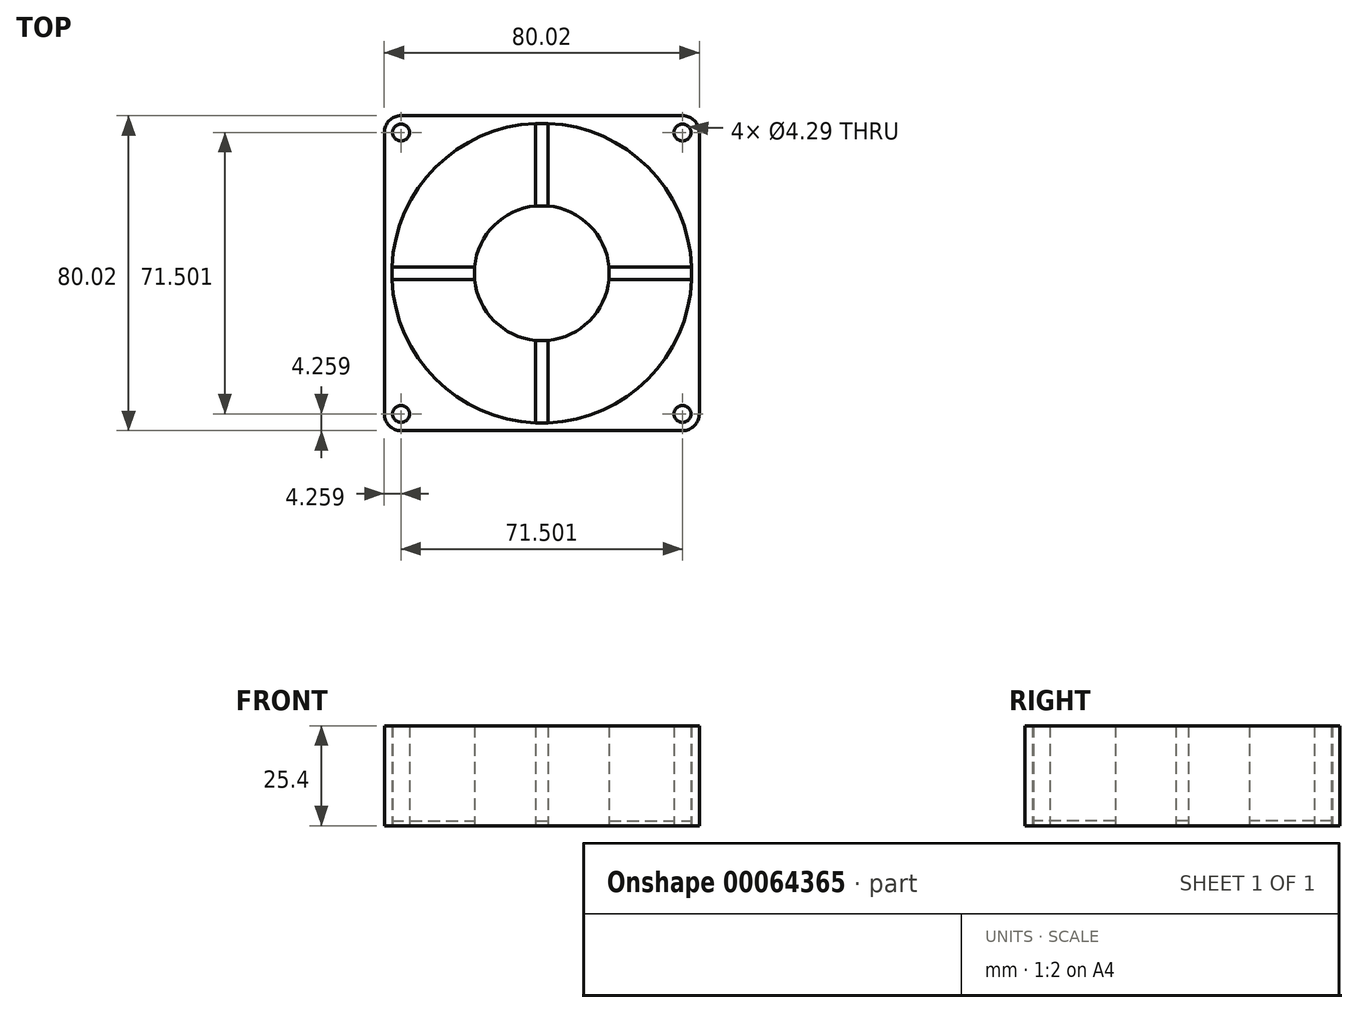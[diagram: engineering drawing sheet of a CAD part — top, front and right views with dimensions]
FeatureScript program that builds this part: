
annotation { "Feature Type Name" : "Feature", "Feature Type Description" : "" }
export const myFeature = defineFeature(function(context is Context, id is Id, definition is map)
    precondition{}
    {
        {
            var Q0;
            Q0=qCreatedBy(makeId("Top.planeOp"),FACE);
            var sketch = newSketch(context, id + "F0", { "sketchPlane" : qUnion([Q0])});
            skLineSegment(sketch, "E0.rect.bottom", {"start": v(-35.74, 40) * mm, "end": v(35.74, 40) * mm});
            skLineSegment(sketch, "E0.rect.top", {"start": v(-35.74, -40) * mm, "end": v(35.74, -40) * mm});
            skLineSegment(sketch, "E0.rect.left", {"start": v(-40, 35.74) * mm, "end": v(-40, -35.74) * mm});
            skLineSegment(sketch, "E0.rect.right", {"start": v(40, 35.74) * mm, "end": v(40, -35.74) * mm});
            skPoint(sketch, "E0.rect.middle", {"position": v(0, 0) * mm});
            skArc(sketch, "E1", {"start": v(-38.07, -1.59) * mm, "mid": v(-26.94, -26.94) * mm, "end": v(-1.59, -38.07) * mm});
            skPoint(sketch, "E2", {"position": v(-35.75, 35.75) * mm});
            skPoint(sketch, "E3", {"position": v(35.75, 35.75) * mm});
            skPoint(sketch, "E4", {"position": v(35.75, -35.75) * mm});
            skPoint(sketch, "E5", {"position": v(-35.75, -35.75) * mm});
            skArc(sketch, "E6.filletArc", {"start": v(-35.74, 40) * mm, "mid": v(-38.76, 38.76) * mm, "end": v(-40, 35.74) * mm});
            skArc(sketch, "E7.filletArc", {"start": v(40, 35.74) * mm, "mid": v(38.76, 38.76) * mm, "end": v(35.74, 40) * mm});
            skArc(sketch, "E8.filletArc", {"start": v(35.74, -40) * mm, "mid": v(38.76, -38.76) * mm, "end": v(40, -35.74) * mm});
            skArc(sketch, "E9.filletArc", {"start": v(-40, -35.74) * mm, "mid": v(-38.76, -38.76) * mm, "end": v(-35.74, -40) * mm});
            skArc(sketch, "E10", {"start": v(-17.07, -1.59) * mm, "mid": v(-12.12, -12.12) * mm, "end": v(-1.59, -17.07) * mm});
            skLineSegment(sketch, "E11", {"start": v(-38.07, 1.59) * mm, "end": v(-17.07, 1.59) * mm});
            skLineSegment(sketch, "E12", {"start": v(-38.07, -1.59) * mm, "end": v(-17.07, -1.59) * mm});
            skLineSegment(sketch, "E13.trimOffspring", {"start": v(17.07, 1.59) * mm, "end": v(38.07, 1.59) * mm});
            skLineSegment(sketch, "E14.trimOffspring", {"start": v(17.07, -1.59) * mm, "end": v(38.07, -1.59) * mm});
            skArc(sketch, "E15.trimOffspring", {"start": v(17.07, 1.59) * mm, "mid": v(12.12, 12.12) * mm, "end": v(1.58, 17.07) * mm});
            skArc(sketch, "E16.trimOffspring", {"start": v(38.07, 1.59) * mm, "mid": v(26.94, 26.94) * mm, "end": v(1.58, 38.07) * mm});
            skLineSegment(sketch, "E17", {"start": v(-1.59, 38.07) * mm, "end": v(-1.59, 17.07) * mm});
            skLineSegment(sketch, "E18.trimOffspring", {"start": v(1.58, 38.07) * mm, "end": v(1.58, 17.07) * mm});
            skLineSegment(sketch, "E19.trimOffspring", {"start": v(-1.59, -17.07) * mm, "end": v(-1.59, -38.07) * mm});
            skLineSegment(sketch, "E20.trimOffspring", {"start": v(1.58, -17.07) * mm, "end": v(1.58, -38.07) * mm});
            skArc(sketch, "E21.trimOffspring", {"start": v(-1.59, 17.07) * mm, "mid": v(-12.12, 12.12) * mm, "end": v(-17.07, 1.59) * mm});
            skArc(sketch, "E22.trimOffspring", {"start": v(1.58, -17.07) * mm, "mid": v(12.12, -12.12) * mm, "end": v(17.07, -1.59) * mm});
            skArc(sketch, "E23.trimOffspring", {"start": v(1.58, -38.07) * mm, "mid": v(26.94, -26.94) * mm, "end": v(38.07, -1.59) * mm});
            skArc(sketch, "E24.trimOffspring", {"start": v(-1.59, 38.07) * mm, "mid": v(-26.94, 26.94) * mm, "end": v(-38.07, 1.59) * mm});
            skSolve(sketch);
        }
        {
            var Q0;
            Q0 = qSketchRegion(id + "F0", true);
            var Q1;
            Q1=makeQuery(id+"F0.imprint","IMPRINT",FACE,{"disambiguationData":[TD([[makeQuery(id+"F0.imprint","IMPRINT",EDGE,{"derivedFrom":sQuery(id+"F0.wireOp",EDGE,"E10")}),1.0]])]});
            extrude(context, id + "F1", {"entities" : qUnion([Q0, Q1]), "depth" : 25.4 * mm});
        }
        {
            var Q0;
            Q0=sQuery(id+"F0.wireOp",VERTEX,"E2");
            var Q1;
            Q1=sQuery(id+"F0.wireOp",VERTEX,"E3");
            var Q2;
            Q2=sQuery(id+"F0.wireOp",VERTEX,"E4");
            var Q3;
            Q3=sQuery(id+"F0.wireOp",VERTEX,"E5");
            var Q4;
            Q4=makeQuery(id+"F1.opExtrude","SWEPT_BODY",BODY,{"disambiguationData":[OSD([sQuery(id+"F0.wireOp",EDGE,"E0.rect.bottom"),sQuery(id+"F0.wireOp",EDGE,"E0.rect.top"),sQuery(id+"F0.wireOp",EDGE,"E0.rect.left"),sQuery(id+"F0.wireOp",EDGE,"E0.rect.right"),sQuery(id+"F0.wireOp",EDGE,"E1"),sQuery(id+"F0.wireOp",EDGE,"E6.filletArc"),sQuery(id+"F0.wireOp",EDGE,"E7.filletArc"),sQuery(id+"F0.wireOp",EDGE,"E8.filletArc"),sQuery(id+"F0.wireOp",EDGE,"E9.filletArc")])]});
            hole(context, id + "F2", {"style" : HoleStyle.SIMPLE, "holeDiameter" : 4.3 * mm, "endStyle" : HoleEndStyle.THROUGH, "oppositeDirection" : true, "locations" : qUnion([Q0, Q1, Q2, Q3]), "scope" : qUnion([Q4])});
        }
        {
            var Q0;
            Q0=makeQuery(id+"F1.opExtrude","CAP_FACE",FACE,{"disambiguationData":[OSD([sQuery(id+"F0.wireOp",EDGE,"E0.rect.bottom"),sQuery(id+"F0.wireOp",EDGE,"E0.rect.top"),sQuery(id+"F0.wireOp",EDGE,"E0.rect.left"),sQuery(id+"F0.wireOp",EDGE,"E0.rect.right"),sQuery(id+"F0.wireOp",EDGE,"E1"),sQuery(id+"F0.wireOp",EDGE,"E6.filletArc"),sQuery(id+"F0.wireOp",EDGE,"E7.filletArc"),sQuery(id+"F0.wireOp",EDGE,"E8.filletArc"),sQuery(id+"F0.wireOp",EDGE,"E9.filletArc"),sQuery(id+"F0.wireOp",EDGE,"E10"),sQuery(id+"F0.wireOp",EDGE,"E11"),sQuery(id+"F0.wireOp",EDGE,"E12"),sQuery(id+"F0.wireOp",EDGE,"E13.trimOffspring"),sQuery(id+"F0.wireOp",EDGE,"E14.trimOffspring"),sQuery(id+"F0.wireOp",EDGE,"E15.trimOffspring"),sQuery(id+"F0.wireOp",EDGE,"E16.trimOffspring"),sQuery(id+"F0.wireOp",EDGE,"E17"),sQuery(id+"F0.wireOp",EDGE,"E18.trimOffspring"),sQuery(id+"F0.wireOp",EDGE,"E19.trimOffspring"),sQuery(id+"F0.wireOp",EDGE,"E20.trimOffspring"),sQuery(id+"F0.wireOp",EDGE,"E21.trimOffspring"),sQuery(id+"F0.wireOp",EDGE,"E22.trimOffspring"),sQuery(id+"F0.wireOp",EDGE,"E23.trimOffspring"),sQuery(id+"F0.wireOp",EDGE,"E24.trimOffspring")])],"isStart":false});
            var sketch = newSketch(context, id + "F3", { "sketchPlane" : qUnion([Q0])});
            skLineSegment(sketch, "E25", {"start": v(-38.07, 1.59) * mm, "end": v(-38.07, -1.59) * mm});
            skLineSegment(sketch, "E26", {"start": v(-38.07, -1.59) * mm, "end": v(-17.07, -1.59) * mm});
            skLineSegment(sketch, "E27", {"start": v(-17.07, -1.59) * mm, "end": v(-17.07, 1.59) * mm});
            skLineSegment(sketch, "E28", {"start": v(-17.07, 1.59) * mm, "end": v(-38.07, 1.59) * mm});
            skLineSegment(sketch, "E29", {"start": v(-1.59, 38.07) * mm, "end": v(1.58, 38.07) * mm});
            skLineSegment(sketch, "E30", {"start": v(1.58, 38.07) * mm, "end": v(1.58, 17.07) * mm});
            skLineSegment(sketch, "E31", {"start": v(1.58, 17.07) * mm, "end": v(-1.59, 17.07) * mm});
            skLineSegment(sketch, "E32", {"start": v(38.07, 1.59) * mm, "end": v(38.07, -1.59) * mm});
            skLineSegment(sketch, "E33", {"start": v(38.07, -1.59) * mm, "end": v(17.07, -1.59) * mm});
            skLineSegment(sketch, "E34", {"start": v(17.07, -1.59) * mm, "end": v(17.07, 1.59) * mm});
            skLineSegment(sketch, "E35", {"start": v(17.07, 1.59) * mm, "end": v(38.07, 1.59) * mm});
            skLineSegment(sketch, "E36", {"start": v(1.58, -17.07) * mm, "end": v(1.58, -38.07) * mm});
            skLineSegment(sketch, "E37", {"start": v(-1.59, -38.07) * mm, "end": v(-1.59, -17.07) * mm});
            skLineSegment(sketch, "E38", {"start": v(-1.59, -17.07) * mm, "end": v(1.58, -17.07) * mm});
            skLineSegment(sketch, "E39", {"start": v(1.58, -38.07) * mm, "end": v(-1.59, -38.07) * mm});
            skLineSegment(sketch, "E40", {"start": v(-1.59, 17.07) * mm, "end": v(-1.59, 38.07) * mm});
            skSolve(sketch);
        }
        {
            var Q0;
            Q0 = qSketchRegion(id + "F3", true);
            extrude(context, id + "F4", {"entities" : qUnion([Q0]), "operationType" : NewBodyOperationType.REMOVE, "oppositeDirection" : true, "depth" : 24.13 * mm});
        }
    });
